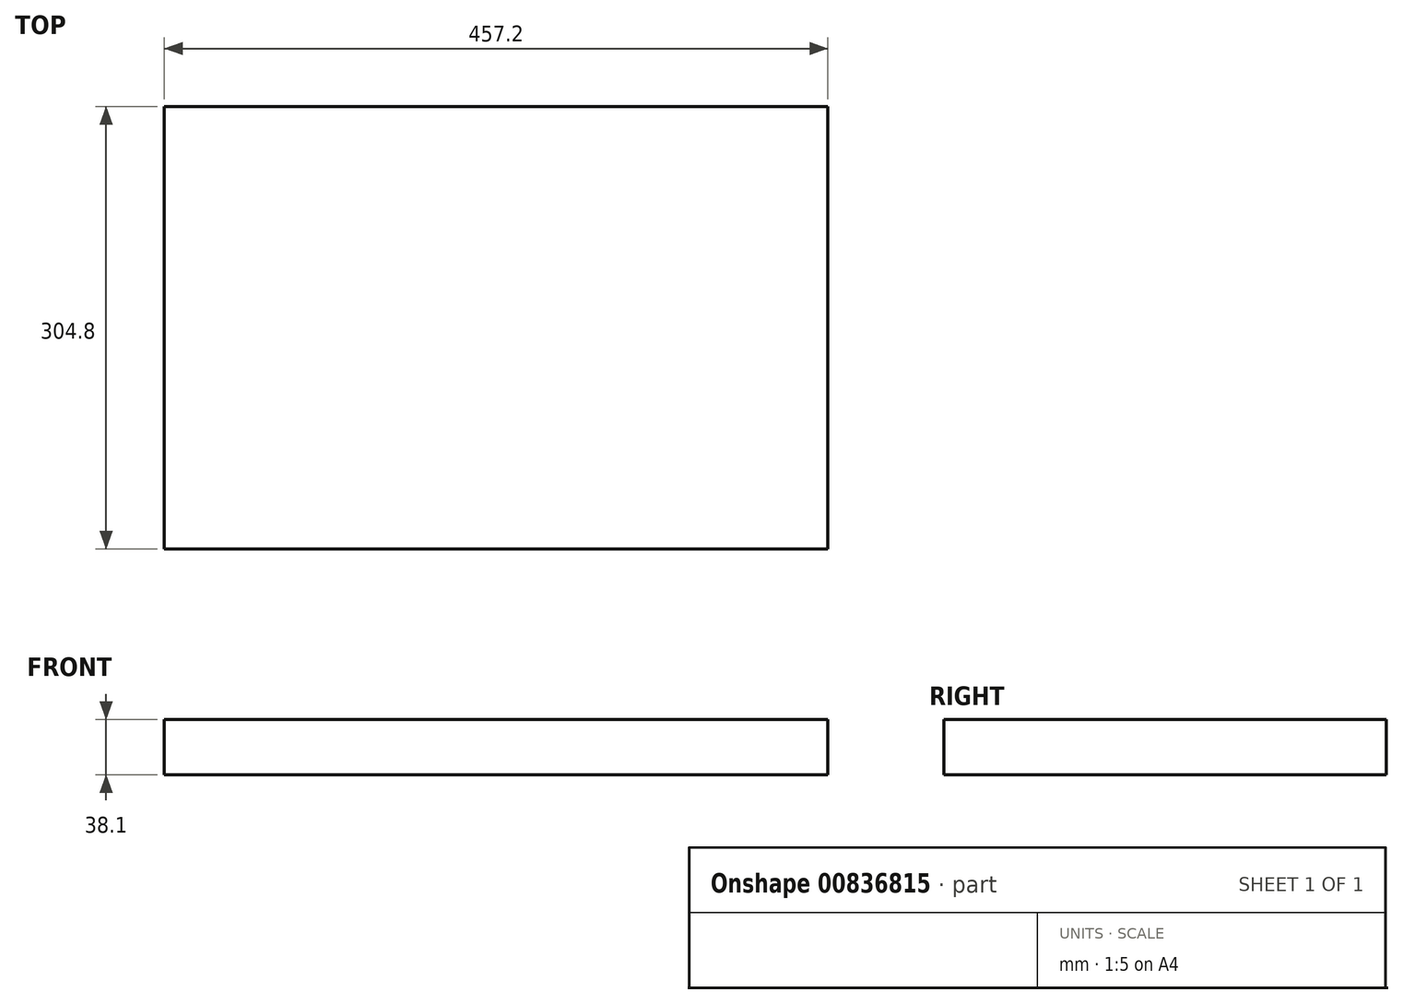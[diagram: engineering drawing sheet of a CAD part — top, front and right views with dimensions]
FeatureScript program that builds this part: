
annotation { "Feature Type Name" : "Feature", "Feature Type Description" : "" }
export const myFeature = defineFeature(function(context is Context, id is Id, definition is map)
    precondition{}
    {
        {
            var Q0;
            Q0=qCreatedBy(makeId("Top.planeOp"),FACE);
            var sketch = newSketch(context, id + "F0", { "sketchPlane" : qUnion([Q0])});
            skLineSegment(sketch, "E0.bottom", {"start": v(-126.81, 196.87) * mm, "end": v(330.39, 196.87) * mm});
            skLineSegment(sketch, "E0.top", {"start": v(-126.81, -107.93) * mm, "end": v(330.39, -107.93) * mm});
            skLineSegment(sketch, "E0.left", {"start": v(-126.81, 196.87) * mm, "end": v(-126.81, -107.93) * mm});
            skLineSegment(sketch, "E0.right", {"start": v(330.39, 196.87) * mm, "end": v(330.39, -107.93) * mm});
            skSolve(sketch);
        }
        {
            var Q0;
            Q0 = qSketchRegion(id + "F0", true);
            extrude(context, id + "F1", {"entities" : qUnion([Q0]), "depth" : 38.1 * mm, "offsetDistance" : 25.4 * mm});
        }
    });
